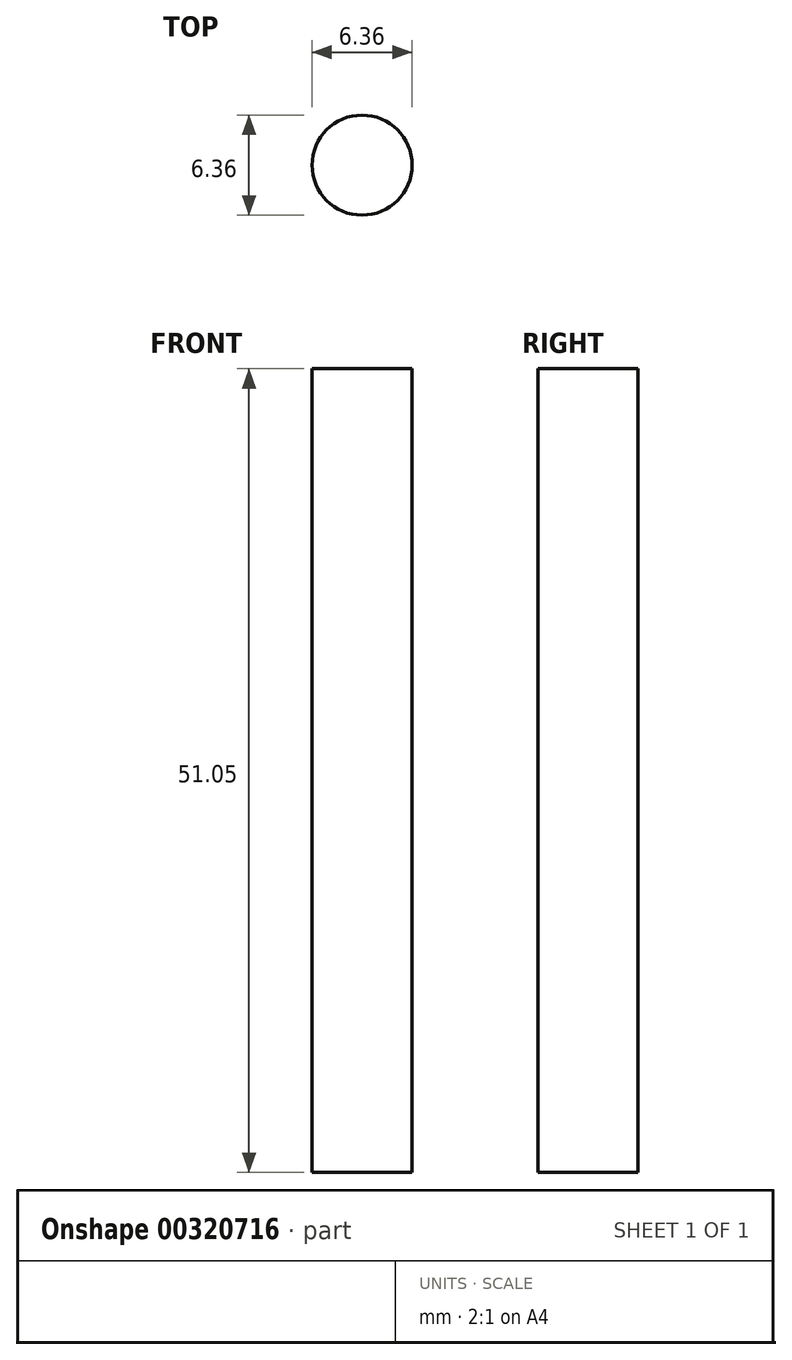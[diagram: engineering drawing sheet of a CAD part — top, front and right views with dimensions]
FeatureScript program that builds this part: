
annotation { "Feature Type Name" : "Feature", "Feature Type Description" : "" }
export const myFeature = defineFeature(function(context is Context, id is Id, definition is map)
    precondition{}
    {
        {
            var Q0;
            Q0=qCreatedBy(makeId("Top.planeOp"),FACE);
            var sketch = newSketch(context, id + "F0", { "sketchPlane" : qUnion([Q0])});
            skCircle(sketch, "E0", {"center": v(0, 0) * mm, "radius": 3.18 * mm});
            skSolve(sketch);
        }
        {
            var Q0;
            Q0 = qSketchRegion(id + "F0", true);
            extrude(context, id + "F1", {"entities" : qUnion([Q0]), "depth" : 57.15 * mm});
        }
        {
            var Q0;
            Q0=makeQuery(id+"F1.opExtrude","CAP_FACE",FACE,{"disambiguationData":[OSD([sQuery(id+"F0.wireOp",EDGE,"E0")])],"isStart":false});
            extrude(context, id + "F2", {"entities" : qUnion([Q0]), "operationType" : NewBodyOperationType.ADD, "oppositeDirection" : true, "depth" : 2.54 * mm});
        }
        {
            var Q0;
            Q0=makeQuery(id+"F1.opExtrude","CAP_FACE",FACE,{"disambiguationData":[OSD([sQuery(id+"F0.wireOp",EDGE,"E0")])],"isStart":false});
            extrude(context, id + "F3", {"entities" : qUnion([Q0]), "operationType" : NewBodyOperationType.REMOVE, "oppositeDirection" : true, "depth" : 3.8 * mm});
        }
        {
            var Q0;
            Q0=makeQuery(id+"F3.boolean.opBoolean","COPY",FACE,{"derivedFrom":makeQuery(id+"F3.opExtrude","CAP_FACE",FACE,{"disambiguationData":[OSD([sQuery(id+"F0.wireOp",EDGE,"E0")])],"isStart":false})});
            extrude(context, id + "F4", {"entities" : qUnion([Q0]), "operationType" : NewBodyOperationType.REMOVE, "oppositeDirection" : true, "depth" : 2.3 * mm});
        }
    });
